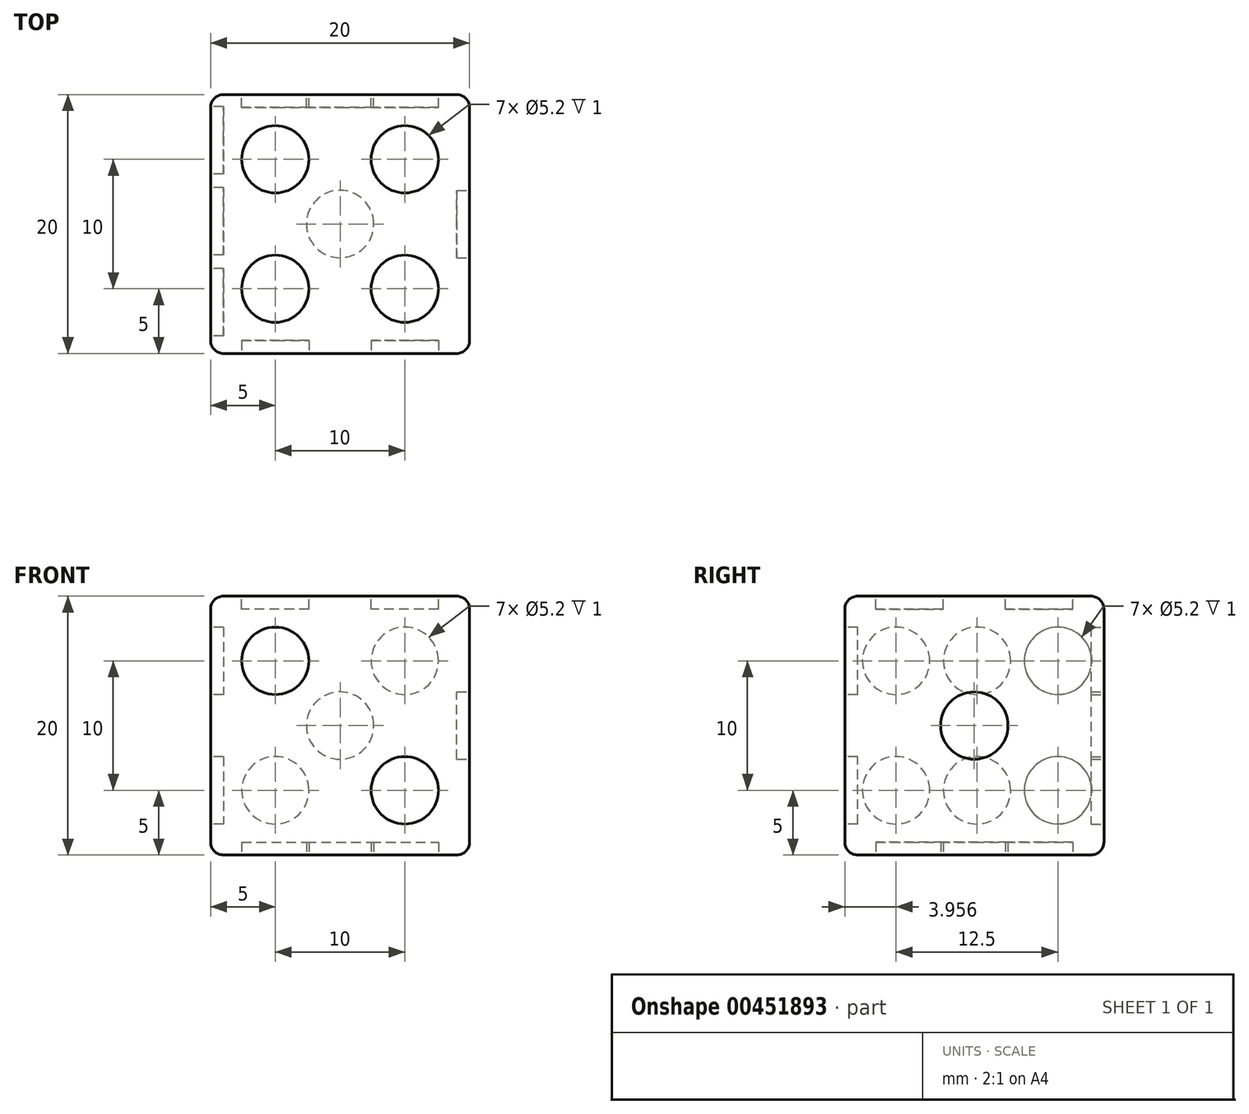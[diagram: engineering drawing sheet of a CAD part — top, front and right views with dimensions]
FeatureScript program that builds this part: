
annotation { "Feature Type Name" : "Feature", "Feature Type Description" : "" }
export const myFeature = defineFeature(function(context is Context, id is Id, definition is map)
    precondition{}
    {
        {
            var Q0;
            Q0=qCreatedBy(makeId("Right.planeOp"),FACE);
            var sketch = newSketch(context, id + "F0", { "sketchPlane" : qUnion([Q0])});
            skLineSegment(sketch, "E0.bottom", {"start": v(0, 0) * mm, "end": v(20, 0) * mm});
            skLineSegment(sketch, "E0.top", {"start": v(0, 20) * mm, "end": v(20, 20) * mm});
            skLineSegment(sketch, "E0.left", {"start": v(0, 0) * mm, "end": v(0, 20) * mm});
            skLineSegment(sketch, "E0.right", {"start": v(20, 0) * mm, "end": v(20, 20) * mm});
            skSolve(sketch);
        }
        {
            var Q0;
            Q0 = qSketchRegion(id + "F0", true);
            extrude(context, id + "F1", {"entities" : qUnion([Q0]), "depth" : 20 * mm});
        }
        {
            var Q0;
            Q0=makeQuery(id+"F1.opExtrude","SWEPT_FACE",FACE,{"disambiguationData":[OSD([sQuery(id+"F0.wireOp",EDGE,"E0.right")])]});
            var sketch = newSketch(context, id + "F2", { "sketchPlane" : qUnion([Q0])});
            skLineSegment(sketch, "E1", {"start": v(-20, 20) * mm, "end": v(0, 0) * mm, "construction": true});
            skLineSegment(sketch, "E2", {"start": v(0, 20) * mm, "end": v(-20, 0) * mm, "construction": true});
            skLineSegment(sketch, "E3", {"start": v(-20, 10) * mm, "end": v(7.09, 10) * mm, "construction": true});
            skLineSegment(sketch, "E4", {"start": v(-10, 20) * mm, "end": v(-10, 0) * mm, "construction": true});
            skCircle(sketch, "E5", {"center": v(-10, 10) * mm, "radius": 2.6 * mm});
            skCircle(sketch, "E6", {"center": v(-15, 15) * mm, "radius": 2.6 * mm});
            skCircle(sketch, "E7.MirrorC", {"center": v(-5, 15) * mm, "radius": 2.6 * mm});
            skCircle(sketch, "E8.MirrorC", {"center": v(-15, 5) * mm, "radius": 2.6 * mm});
            skCircle(sketch, "E9.MirrorC", {"center": v(-5, 5) * mm, "radius": 2.6 * mm});
            skSolve(sketch);
        }
        {
            var Q0;
            Q0 = qSketchRegion(id + "F2", true);
            extrude(context, id + "F3", {"entities" : qUnion([Q0]), "operationType" : NewBodyOperationType.REMOVE, "oppositeDirection" : true, "depth" : 1 * mm});
        }
        {
            var Q0;
            Q0=makeQuery(id+"F1.opExtrude","SWEPT_FACE",FACE,{"disambiguationData":[OSD([sQuery(id+"F0.wireOp",EDGE,"E0.left")])]});
            var sketch = newSketch(context, id + "F4", { "sketchPlane" : qUnion([Q0])});
            skLineSegment(sketch, "E10", {"start": v(0, 0) * mm, "end": v(20, 20) * mm, "construction": true});
            skCircle(sketch, "E11", {"center": v(5, 15) * mm, "radius": 2.6 * mm});
            skCircle(sketch, "E12.MirrorC", {"center": v(15, 5) * mm, "radius": 2.6 * mm});
            skSolve(sketch);
        }
        {
            var Q0;
            Q0 = qSketchRegion(id + "F4", true);
            extrude(context, id + "F5", {"entities" : qUnion([Q0]), "operationType" : NewBodyOperationType.REMOVE, "oppositeDirection" : true, "depth" : 1 * mm});
        }
        {
            var Q0;
            Q0=makeQuery(id+"F1.opExtrude","CAP_FACE",FACE,{"disambiguationData":[OSD([sQuery(id+"F0.wireOp",EDGE,"E0.bottom"),sQuery(id+"F0.wireOp",EDGE,"E0.top"),sQuery(id+"F0.wireOp",EDGE,"E0.left"),sQuery(id+"F0.wireOp",EDGE,"E0.right")])],"isStart":false});
            var sketch = newSketch(context, id + "F6", { "sketchPlane" : qUnion([Q0])});
            skCircle(sketch, "E13", {"center": v(10, 10) * mm, "radius": 2.6 * mm});
            skSolve(sketch);
        }
        {
            var Q0;
            Q0 = qSketchRegion(id + "F6", true);
            extrude(context, id + "F7", {"entities" : qUnion([Q0]), "operationType" : NewBodyOperationType.REMOVE, "oppositeDirection" : true, "depth" : 1 * mm});
        }
        {
            var Q0;
            Q0=makeQuery(id+"F1.opExtrude","SWEPT_FACE",FACE,{"disambiguationData":[OSD([sQuery(id+"F0.wireOp",EDGE,"E0.top")])]});
            var sketch = newSketch(context, id + "F8", { "sketchPlane" : qUnion([Q0])});
            skLineSegment(sketch, "E14", {"start": v(0, 10) * mm, "end": v(20, 10) * mm, "construction": true});
            skLineSegment(sketch, "E15", {"start": v(20, 10) * mm, "end": v(20, 0) * mm, "construction": true});
            skLineSegment(sketch, "E16", {"start": v(20, 0) * mm, "end": v(0, 20) * mm, "construction": true});
            skLineSegment(sketch, "E17", {"start": v(0, 20) * mm, "end": v(20, 20) * mm, "construction": true});
            skLineSegment(sketch, "E18", {"start": v(20, 20) * mm, "end": v(0, 0) * mm, "construction": true});
            skLineSegment(sketch, "E19", {"start": v(0, 0) * mm, "end": v(10, 0) * mm, "construction": true});
            skLineSegment(sketch, "E20", {"start": v(10, 0) * mm, "end": v(10, 20) * mm, "construction": true});
            skCircle(sketch, "E21", {"center": v(5, 5) * mm, "radius": 2.6 * mm});
            skCircle(sketch, "E22.MirrorC", {"center": v(5, 15) * mm, "radius": 2.6 * mm});
            skCircle(sketch, "E23.MirrorC", {"center": v(15, 5) * mm, "radius": 2.6 * mm});
            skCircle(sketch, "E24.MirrorC", {"center": v(15, 15) * mm, "radius": 2.6 * mm});
            skSolve(sketch);
        }
        {
            var Q0;
            Q0 = qSketchRegion(id + "F8", true);
            extrude(context, id + "F9", {"entities" : qUnion([Q0]), "operationType" : NewBodyOperationType.REMOVE, "oppositeDirection" : true, "depth" : 1 * mm});
        }
        {
            var Q0;
            Q0=makeQuery(id+"F1.opExtrude","SWEPT_FACE",FACE,{"disambiguationData":[OSD([sQuery(id+"F0.wireOp",EDGE,"E0.bottom")])]});
            var sketch = newSketch(context, id + "F10", { "sketchPlane" : qUnion([Q0])});
            skCircle(sketch, "E25", {"center": v(10, -10) * mm, "radius": 2.6 * mm});
            skPoint(sketch, "E25.centerSnap0", {"position": v(10, -20) * mm});
            skPoint(sketch, "E25.centerSnap1", {"position": v(0, -10) * mm});
            skCircle(sketch, "E26", {"center": v(5, -5) * mm, "radius": 2.6 * mm});
            skLineSegment(sketch, "E27", {"start": v(0, -20) * mm, "end": v(20, 0) * mm, "construction": true});
            skCircle(sketch, "E28.MirrorC", {"center": v(15, -15) * mm, "radius": 2.6 * mm});
            skSolve(sketch);
        }
        {
            var Q0;
            Q0 = qSketchRegion(id + "F10", true);
            extrude(context, id + "F11", {"entities" : qUnion([Q0]), "operationType" : NewBodyOperationType.REMOVE, "oppositeDirection" : true, "depth" : 1 * mm});
        }
        {
            var Q0;
            Q0=makeQuery(id+"F1.opExtrude","CAP_FACE",FACE,{"disambiguationData":[OSD([sQuery(id+"F0.wireOp",EDGE,"E0.bottom"),sQuery(id+"F0.wireOp",EDGE,"E0.top"),sQuery(id+"F0.wireOp",EDGE,"E0.left"),sQuery(id+"F0.wireOp",EDGE,"E0.right")])],"isStart":true});
            var sketch = newSketch(context, id + "F12", { "sketchPlane" : qUnion([Q0])});
            skCircle(sketch, "E29", {"center": v(-3.96, 15) * mm, "radius": 2.6 * mm});
            skCircle(sketch, "E30", {"center": v(-10.2, 15) * mm, "radius": 2.6 * mm});
            skCircle(sketch, "E31", {"center": v(-16.46, 15) * mm, "radius": 2.6 * mm});
            skLineSegment(sketch, "E32", {"start": v(0, 10) * mm, "end": v(-20, 10) * mm, "construction": true});
            skCircle(sketch, "E33.MirrorC", {"center": v(-16.46, 5) * mm, "radius": 2.6 * mm});
            skCircle(sketch, "E34.MirrorC", {"center": v(-10.2, 5) * mm, "radius": 2.6 * mm});
            skCircle(sketch, "E35.MirrorC", {"center": v(-3.96, 5) * mm, "radius": 2.6 * mm});
            skSolve(sketch);
        }
        {
            var Q0;
            Q0 = qSketchRegion(id + "F12", true);
            extrude(context, id + "F13", {"entities" : qUnion([Q0]), "operationType" : NewBodyOperationType.REMOVE, "oppositeDirection" : true, "depth" : 1 * mm});
        }
        {
            var Q0;
            Q0=makeQuery(id+"F1.opExtrude","SWEPT_EDGE",EDGE,{"disambiguationData":[OSD([sQuery(id+"F0.wireOp",EDGE,"E0.bottom"),sQuery(id+"F0.wireOp",EDGE,"E0.left")])]});
            var Q1;
            Q1=makeQuery(id+"F1.opExtrude","CAP_EDGE",EDGE,{"disambiguationData":[OSD([sQuery(id+"F0.wireOp",EDGE,"E0.bottom")])],"isStart":false});
            var Q2;
            Q2=makeQuery(id+"F1.opExtrude","CAP_EDGE",EDGE,{"disambiguationData":[OSD([sQuery(id+"F0.wireOp",EDGE,"E0.left")])],"isStart":false});
            var Q3;
            Q3=makeQuery(id+"F1.opExtrude","CAP_EDGE",EDGE,{"disambiguationData":[OSD([sQuery(id+"F0.wireOp",EDGE,"E0.top")])],"isStart":false});
            var Q4;
            Q4=makeQuery(id+"F1.opExtrude","SWEPT_EDGE",EDGE,{"disambiguationData":[OSD([sQuery(id+"F0.wireOp",EDGE,"E0.top"),sQuery(id+"F0.wireOp",EDGE,"E0.left")])]});
            var Q5;
            Q5=makeQuery(id+"F1.opExtrude","CAP_EDGE",EDGE,{"disambiguationData":[OSD([sQuery(id+"F0.wireOp",EDGE,"E0.top")])],"isStart":true});
            var Q6;
            Q6=makeQuery(id+"F1.opExtrude","CAP_EDGE",EDGE,{"disambiguationData":[OSD([sQuery(id+"F0.wireOp",EDGE,"E0.left")])],"isStart":true});
            var Q7;
            Q7=makeQuery(id+"F1.opExtrude","CAP_EDGE",EDGE,{"disambiguationData":[OSD([sQuery(id+"F0.wireOp",EDGE,"E0.right")])],"isStart":true});
            var Q8;
            Q8=makeQuery(id+"F1.opExtrude","SWEPT_EDGE",EDGE,{"disambiguationData":[OSD([sQuery(id+"F0.wireOp",EDGE,"E0.bottom"),sQuery(id+"F0.wireOp",EDGE,"E0.right")])]});
            var Q9;
            Q9=makeQuery(id+"F1.opExtrude","CAP_EDGE",EDGE,{"disambiguationData":[OSD([sQuery(id+"F0.wireOp",EDGE,"E0.right")])],"isStart":false});
            var Q10;
            Q10=makeQuery(id+"F1.opExtrude","SWEPT_EDGE",EDGE,{"disambiguationData":[OSD([sQuery(id+"F0.wireOp",EDGE,"E0.top"),sQuery(id+"F0.wireOp",EDGE,"E0.right")])]});
            var Q11;
            Q11=makeQuery(id+"F1.opExtrude","CAP_EDGE",EDGE,{"disambiguationData":[OSD([sQuery(id+"F0.wireOp",EDGE,"E0.bottom")])],"isStart":true});
            fillet(context, id + "F14", {"entities" : qUnion([Q0, Q1, Q2, Q3, Q4, Q5, Q6, Q7, Q8, Q9, Q10, Q11]), "radius" : 1 * mm, "tangentPropagation" : true, "allowEdgeOverflow" : false});
        }
    });
